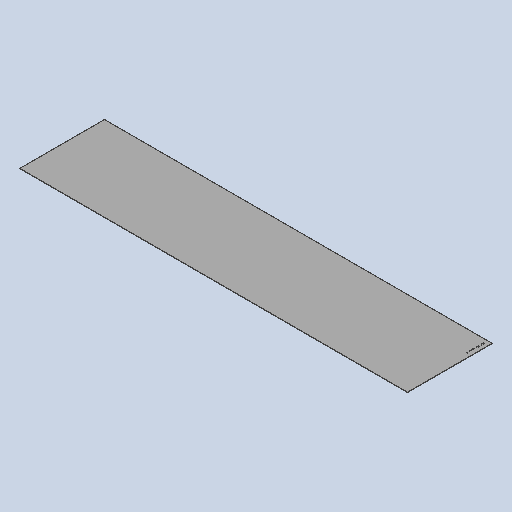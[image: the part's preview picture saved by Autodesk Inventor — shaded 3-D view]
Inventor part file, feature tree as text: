
AUTODESK INVENTOR PART (.ipt)
format: ipt  version: 2025 (Build 290162010, 162A)  size: 173,568 bytes
history: native  units: mm
features: other x3, sketch x2, sheet_metal_op x1
ambient origin geometry x8: Origin, YZ Plane, XZ Plane, XY Plane, X Axis, Y Axis, Z Axis, Center Point
bodies: Solid1 (feature_tree)
feature tree (6):
  sheet_metal_op  "Face1"
  other  "Mark1"
  sketch  "Sketch1"  dims[d0=2748.0mm]
  other  "Plate1"
  sketch  "Sketch5"  dims[d1=600.0mm d2=3.0mm d28=200.0mm d29=15.0mm d30=25.0mm d31=25.0mm]
  other  "Definition1"
